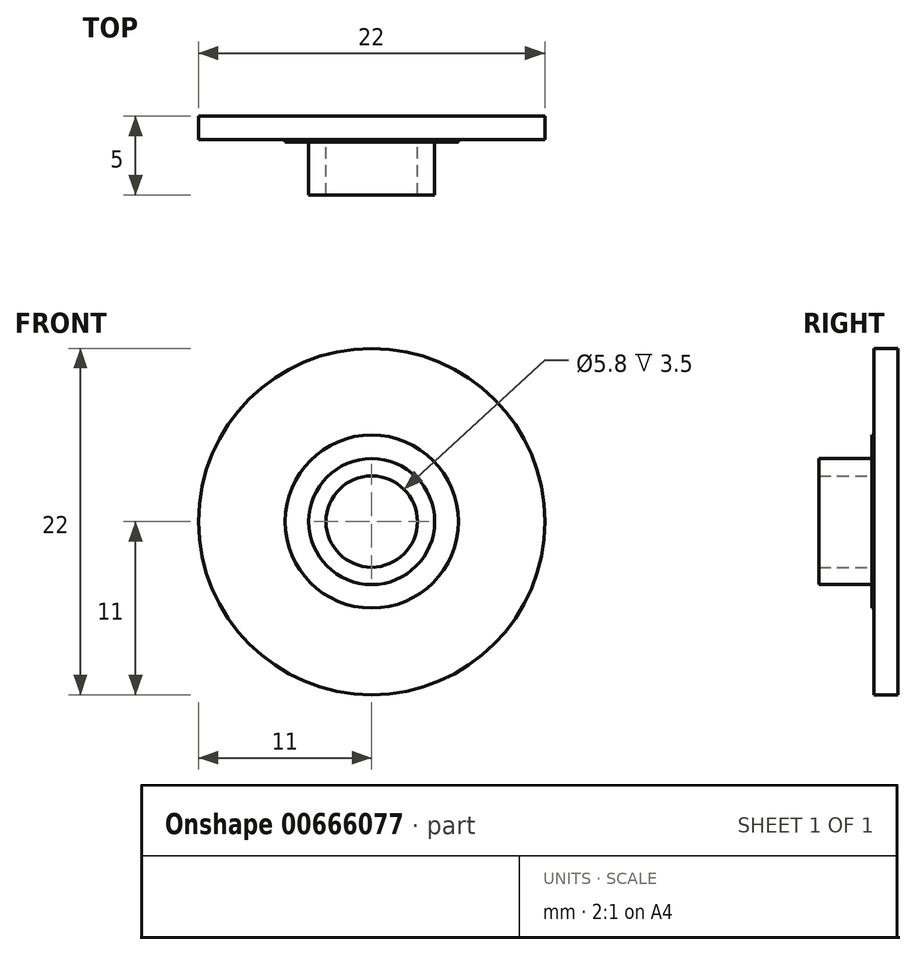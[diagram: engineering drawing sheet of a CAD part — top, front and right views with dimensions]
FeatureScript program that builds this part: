
annotation { "Feature Type Name" : "Feature", "Feature Type Description" : "" }
export const myFeature = defineFeature(function(context is Context, id is Id, definition is map)
    precondition{}
    {
        {
            var Q0;
            Q0=qCreatedBy(makeId("Front.planeOp"),FACE);
            var sketch = newSketch(context, id + "F0", { "sketchPlane" : qUnion([Q0])});
            skCircle(sketch, "E0", {"center": v(0, 0) * mm, "radius": 11 * mm});
            skCircle(sketch, "E1", {"center": v(0, 0) * mm, "radius": 5.5 * mm});
            skCircle(sketch, "E2", {"center": v(0, 0) * mm, "radius": 4 * mm});
            skCircle(sketch, "E3", {"center": v(0, 0) * mm, "radius": 2.9 * mm});
            skSolve(sketch);
        }
        {
            var Q0;
            Q0 = qSketchRegion(id + "F0", true);
            var Q1;
            Q1=makeQuery(id+"F0.imprint","IMPRINT",FACE,{"disambiguationData":[TD([[makeQuery(id+"F0.imprint","IMPRINT",EDGE,{"derivedFrom":sQuery(id+"F0.wireOp",EDGE,"E1")}),1.0]])]});
            var Q2;
            Q2=makeQuery(id+"F0.imprint","IMPRINT",FACE,{"disambiguationData":[TD([[makeQuery(id+"F0.imprint","IMPRINT",EDGE,{"derivedFrom":sQuery(id+"F0.wireOp",EDGE,"E2")}),1.0]])]});
            var Q3;
            Q3=makeQuery(id+"F0.imprint","IMPRINT",FACE,{"disambiguationData":[TD([[makeQuery(id+"F0.imprint","IMPRINT",EDGE,{"derivedFrom":sQuery(id+"F0.wireOp",EDGE,"E3")}),1.0]])]});
            extrude(context, id + "F1", {"entities" : qUnion([Q0, Q1, Q2, Q3]), "depth" : 1.5 * mm, "offsetDistance" : 25 * mm});
        }
        {
            var Q0;
            Q0=makeQuery(id+"F0.imprint","IMPRINT",FACE,{"disambiguationData":[TD([[makeQuery(id+"F0.imprint","IMPRINT",EDGE,{"derivedFrom":sQuery(id+"F0.wireOp",EDGE,"E1")}),1.0]])]});
            extrude(context, id + "F2", {"entities" : qUnion([Q0]), "operationType" : NewBodyOperationType.ADD, "depth" : 1.65 * mm, "offsetDistance" : 25 * mm});
        }
        {
            var Q0;
            Q0=makeQuery(id+"F0.imprint","IMPRINT",FACE,{"disambiguationData":[TD([[makeQuery(id+"F0.imprint","IMPRINT",EDGE,{"derivedFrom":sQuery(id+"F0.wireOp",EDGE,"E2")}),1.0]])]});
            extrude(context, id + "F3", {"entities" : qUnion([Q0]), "operationType" : NewBodyOperationType.ADD, "depth" : 5 * mm, "offsetDistance" : 25 * mm});
        }
    });
